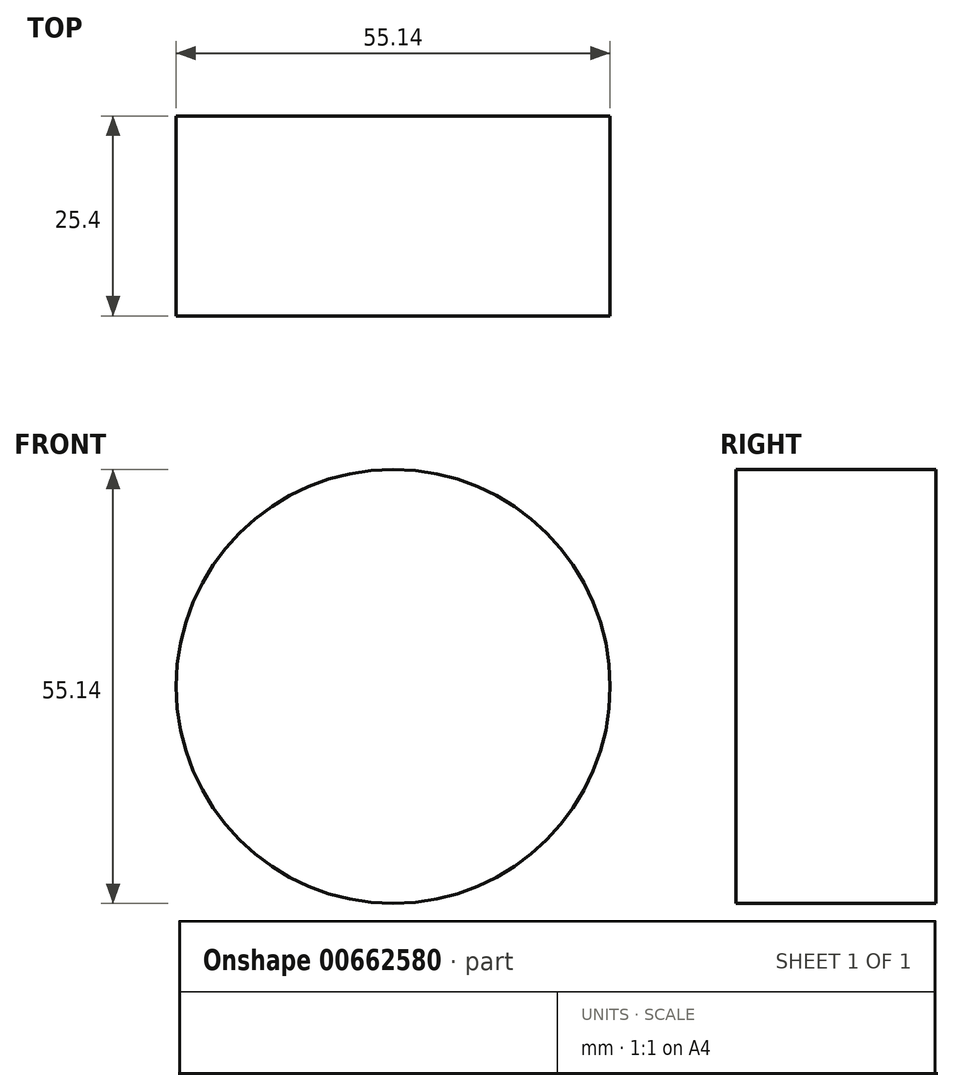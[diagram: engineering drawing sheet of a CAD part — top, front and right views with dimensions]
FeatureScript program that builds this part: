
annotation { "Feature Type Name" : "Feature", "Feature Type Description" : "" }
export const myFeature = defineFeature(function(context is Context, id is Id, definition is map)
    precondition{}
    {
        {
            var Q0;
            Q0=qCreatedBy(makeId("Front.planeOp"),FACE);
            var sketch = newSketch(context, id + "F0", { "sketchPlane" : qUnion([Q0])});
            skCircle(sketch, "E0", {"center": v(0, 0) * mm, "radius": 27.57 * mm});
            skSolve(sketch);
        }
        {
            var Q0;
            Q0=makeQuery(id+"F0.imprint","IMPRINT",FACE,{"disambiguationData":[TD([[makeQuery(id+"F0.imprint","IMPRINT",EDGE,{"derivedFrom":sQuery(id+"F0.wireOp",EDGE,"E0")}),1.0]])]});
            extrude(context, id + "F1", {"entities" : qUnion([Q0]), "depth" : 25.4 * mm, "offsetDistance" : 25.4 * mm});
        }
    });
